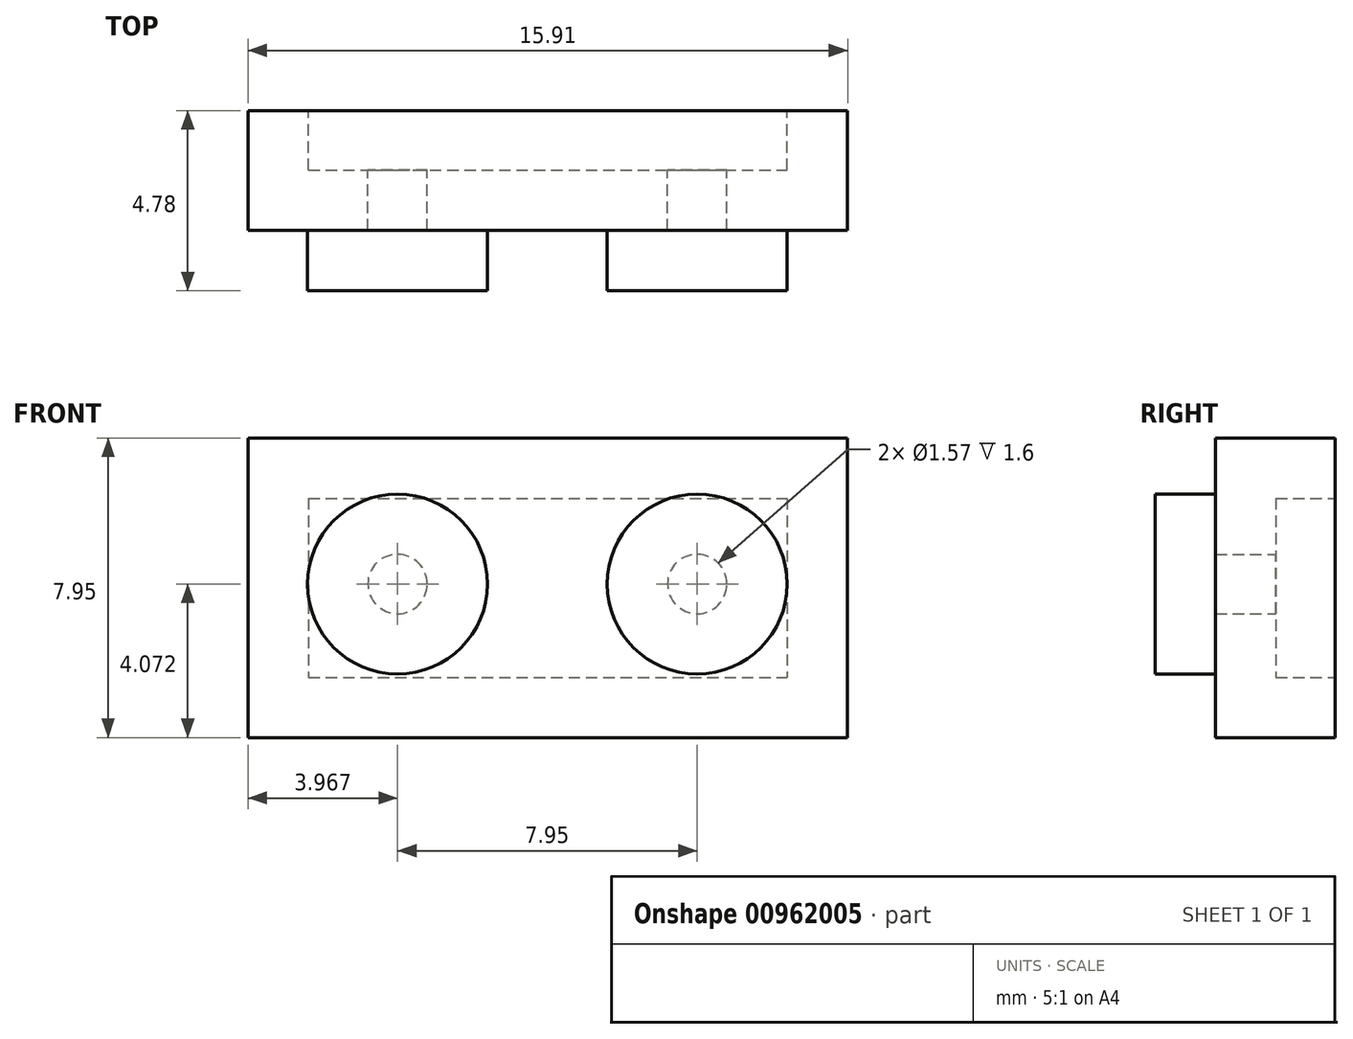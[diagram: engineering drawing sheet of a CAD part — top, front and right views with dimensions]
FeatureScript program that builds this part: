
annotation { "Feature Type Name" : "Feature", "Feature Type Description" : "" }
export const myFeature = defineFeature(function(context is Context, id is Id, definition is map)
    precondition{}
    {
        {
            var Q0;
            Q0=qCreatedBy(makeId("Front.planeOp"),FACE);
            var sketch = newSketch(context, id + "F0", { "sketchPlane" : qUnion([Q0])});
            skLineSegment(sketch, "E0.bottom", {"start": v(-1.98, -20.4) * mm, "end": v(13.93, -20.4) * mm});
            skLineSegment(sketch, "E0.top", {"start": v(-1.98, -28.35) * mm, "end": v(13.93, -28.35) * mm});
            skLineSegment(sketch, "E0.left", {"start": v(-1.98, -20.4) * mm, "end": v(-1.98, -28.35) * mm});
            skLineSegment(sketch, "E0.right", {"start": v(13.93, -20.4) * mm, "end": v(13.93, -28.35) * mm});
            skCircle(sketch, "E1", {"center": v(1.99, -24.28) * mm, "radius": 2.39 * mm});
            skCircle(sketch, "E2.1.0.0", {"center": v(9.94, -24.28) * mm, "radius": 2.39 * mm});
            skLineSegment(sketch, "E2.direction1", {"start": v(1.99, -24.28) * mm, "end": v(9.94, -24.28) * mm, "construction": true});
            skSolve(sketch);
        }
        {
            var Q0;
            Q0=makeQuery(id+"F0.imprint","IMPRINT",FACE,{"disambiguationData":[TD([[makeQuery(id+"F0.imprint","IMPRINT",EDGE,{"derivedFrom":sQuery(id+"F0.wireOp",EDGE,"E0.bottom")}),-1.0]])]});
            extrude(context, id + "F1", {"entities" : qUnion([Q0]), "depth" : 3.17 * mm, "offsetDistance" : 25.4 * mm});
        }
        {
            var Q0;
            Q0=makeQuery(id+"F0.imprint","IMPRINT",FACE,{"disambiguationData":[TD([[makeQuery(id+"F0.imprint","IMPRINT",EDGE,{"derivedFrom":sQuery(id+"F0.wireOp",EDGE,"E1")}),1.0]])]});
            var Q1;
            Q1=makeQuery(id+"F0.imprint","IMPRINT",FACE,{"disambiguationData":[TD([[makeQuery(id+"F0.imprint","IMPRINT",EDGE,{"derivedFrom":sQuery(id+"F0.wireOp",EDGE,"E2.1.0.0")}),1.0]])]});
            extrude(context, id + "F2", {"entities" : qUnion([Q0, Q1]), "operationType" : NewBodyOperationType.ADD, "depth" : 4.78 * mm, "offsetDistance" : 25.4 * mm});
        }
        {
            var Q0;
            {var subQ0=sQuery(id+"F0.wireOp",EDGE,"E2.1.0.0");var subQ1=sQuery(id+"F0.wireOp",EDGE,"E1");Q0=makeQuery(id+"F2.boolean.opBoolean","MERGE",FACE,{"derivedFrom":[makeQuery(id+"F1.opExtrude","CAP_FACE",FACE,{"disambiguationData":[OSD([sQuery(id+"F0.wireOp",EDGE,"E0.bottom"),sQuery(id+"F0.wireOp",EDGE,"E0.top"),sQuery(id+"F0.wireOp",EDGE,"E0.left"),sQuery(id+"F0.wireOp",EDGE,"E0.right"),subQ1,subQ0])],"isStart":true}),makeQuery(id+"F2.opExtrude","CAP_FACE",FACE,{"disambiguationData":[OSD([subQ1])],"isStart":true}),makeQuery(id+"F2.opExtrude","CAP_FACE",FACE,{"disambiguationData":[OSD([subQ0])],"isStart":true})]});}
            shell(context, id + "F3", {"entities" : qUnion([Q0]), "thickness" : 1.6 * mm});
        }
    });
